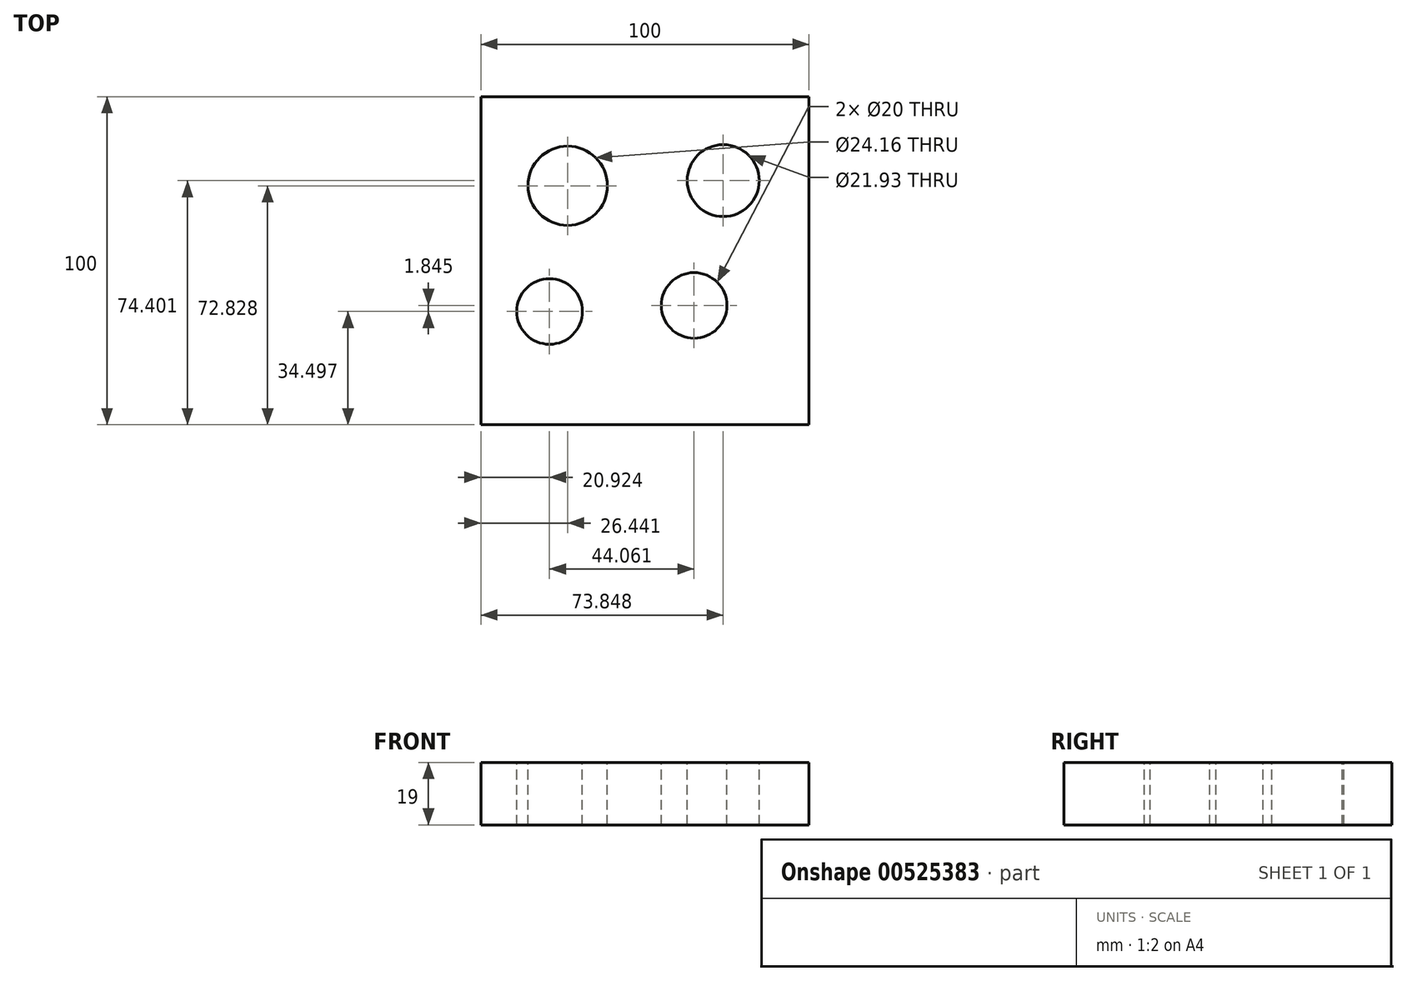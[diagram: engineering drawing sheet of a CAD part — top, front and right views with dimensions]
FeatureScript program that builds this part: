
annotation { "Feature Type Name" : "Feature", "Feature Type Description" : "" }
export const myFeature = defineFeature(function(context is Context, id is Id, definition is map)
    precondition{}
    {
        {
            var Q0;
            Q0=qCreatedBy(makeId("Top.planeOp"),FACE);
            var sketch = newSketch(context, id + "F0", { "sketchPlane" : qUnion([Q0])});
            skLineSegment(sketch, "E0.bottom", {"start": v(-85.73, 37.17) * mm, "end": v(14.27, 37.17) * mm});
            skLineSegment(sketch, "E0.top", {"start": v(-85.73, -62.83) * mm, "end": v(14.27, -62.83) * mm});
            skLineSegment(sketch, "E0.left", {"start": v(-85.73, 37.17) * mm, "end": v(-85.73, -62.83) * mm});
            skLineSegment(sketch, "E0.right", {"start": v(14.27, 37.17) * mm, "end": v(14.27, -62.83) * mm});
            skSolve(sketch);
        }
        {
            var Q0;
            Q0=makeQuery(id+"F0.imprint","IMPRINT",FACE,{"disambiguationData":[TD([[makeQuery(id+"F0.imprint","IMPRINT",EDGE,{"derivedFrom":sQuery(id+"F0.wireOp",EDGE,"E0.bottom")}),-1.0]])]});
            extrude(context, id + "F1", {"entities" : qUnion([Q0]), "depth" : 19 * mm, "offsetDistance" : 25 * mm});
        }
        {
            var Q0;
            Q0=makeQuery(id+"F1.opExtrude","CAP_FACE",FACE,{"disambiguationData":[OSD([sQuery(id+"F0.wireOp",EDGE,"E0.bottom"),sQuery(id+"F0.wireOp",EDGE,"E0.top"),sQuery(id+"F0.wireOp",EDGE,"E0.left"),sQuery(id+"F0.wireOp",EDGE,"E0.right")])],"isStart":false});
            var sketch = newSketch(context, id + "F2", { "sketchPlane" : qUnion([Q0])});
            skCircle(sketch, "E1", {"center": v(-59.29, 10) * mm, "radius": 12.08 * mm});
            skSolve(sketch);
        }
        {
            var Q0;
            Q0 = qSketchRegion(id + "F2", true);
            extrude(context, id + "F3", {"entities" : qUnion([Q0]), "operationType" : NewBodyOperationType.REMOVE, "oppositeDirection" : true, "depth" : 19 * mm, "offsetDistance" : 25 * mm});
        }
        {
            var Q0;
            Q0=makeQuery(id+"F1.opExtrude","CAP_FACE",FACE,{"disambiguationData":[OSD([sQuery(id+"F0.wireOp",EDGE,"E0.bottom"),sQuery(id+"F0.wireOp",EDGE,"E0.top"),sQuery(id+"F0.wireOp",EDGE,"E0.left"),sQuery(id+"F0.wireOp",EDGE,"E0.right")])],"isStart":false});
            var sketch = newSketch(context, id + "F4", { "sketchPlane" : qUnion([Q0])});
            skCircle(sketch, "E2", {"center": v(-11.88, 11.57) * mm, "radius": 10.96 * mm});
            skSolve(sketch);
        }
        {
            var Q0;
            Q0 = qSketchRegion(id + "F4", true);
            extrude(context, id + "F5", {"entities" : qUnion([Q0]), "operationType" : NewBodyOperationType.REMOVE, "oppositeDirection" : true, "depth" : 19 * mm, "offsetDistance" : 25 * mm});
        }
        {
            var Q0;
            Q0=makeQuery(id+"F1.opExtrude","CAP_FACE",FACE,{"disambiguationData":[OSD([sQuery(id+"F0.wireOp",EDGE,"E0.bottom"),sQuery(id+"F0.wireOp",EDGE,"E0.top"),sQuery(id+"F0.wireOp",EDGE,"E0.left"),sQuery(id+"F0.wireOp",EDGE,"E0.right")])],"isStart":false});
            var sketch = newSketch(context, id + "F6", { "sketchPlane" : qUnion([Q0])});
            skCircle(sketch, "E3", {"center": v(-64.8, -28.33) * mm, "radius": 10 * mm});
            skCircle(sketch, "E4", {"center": v(-20.74, -26.49) * mm, "radius": 10 * mm});
            skSolve(sketch);
        }
        {
            var Q0;
            Q0 = qSketchRegion(id + "F6", true);
            extrude(context, id + "F7", {"entities" : qUnion([Q0]), "operationType" : NewBodyOperationType.REMOVE, "oppositeDirection" : true, "depth" : 19 * mm, "offsetDistance" : 25 * mm});
        }
    });
